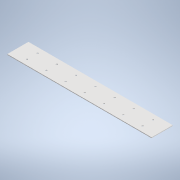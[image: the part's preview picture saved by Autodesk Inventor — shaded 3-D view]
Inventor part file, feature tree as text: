
AUTODESK INVENTOR PART (.ipt)
format: ipt  version: 2022 (Build 260153000, 153)  size: 129,024 bytes
history: native  units: mm
features: sheet_metal_op x1, sketch x1, other x1
ambient origin geometry x8: Origin, YZ Plane, XZ Plane, XY Plane, X Axis, Y Axis, Z Axis, Center Point
bodies: Solid1 (feature_tree)
feature tree (3):
  sheet_metal_op  "Face1"
  sketch  "Sketch1"  dims[d0=44.0mm d1=300.0mm d2=3.35mm d3=11.0mm d4=3.35mm d5=30.0mm d6=30.0mm d7=11.0mm d8=70.0mm d10=40.0mm d11=10.0mm d13=10.0mm d15=1.5mm]
  other  "Plate1"
